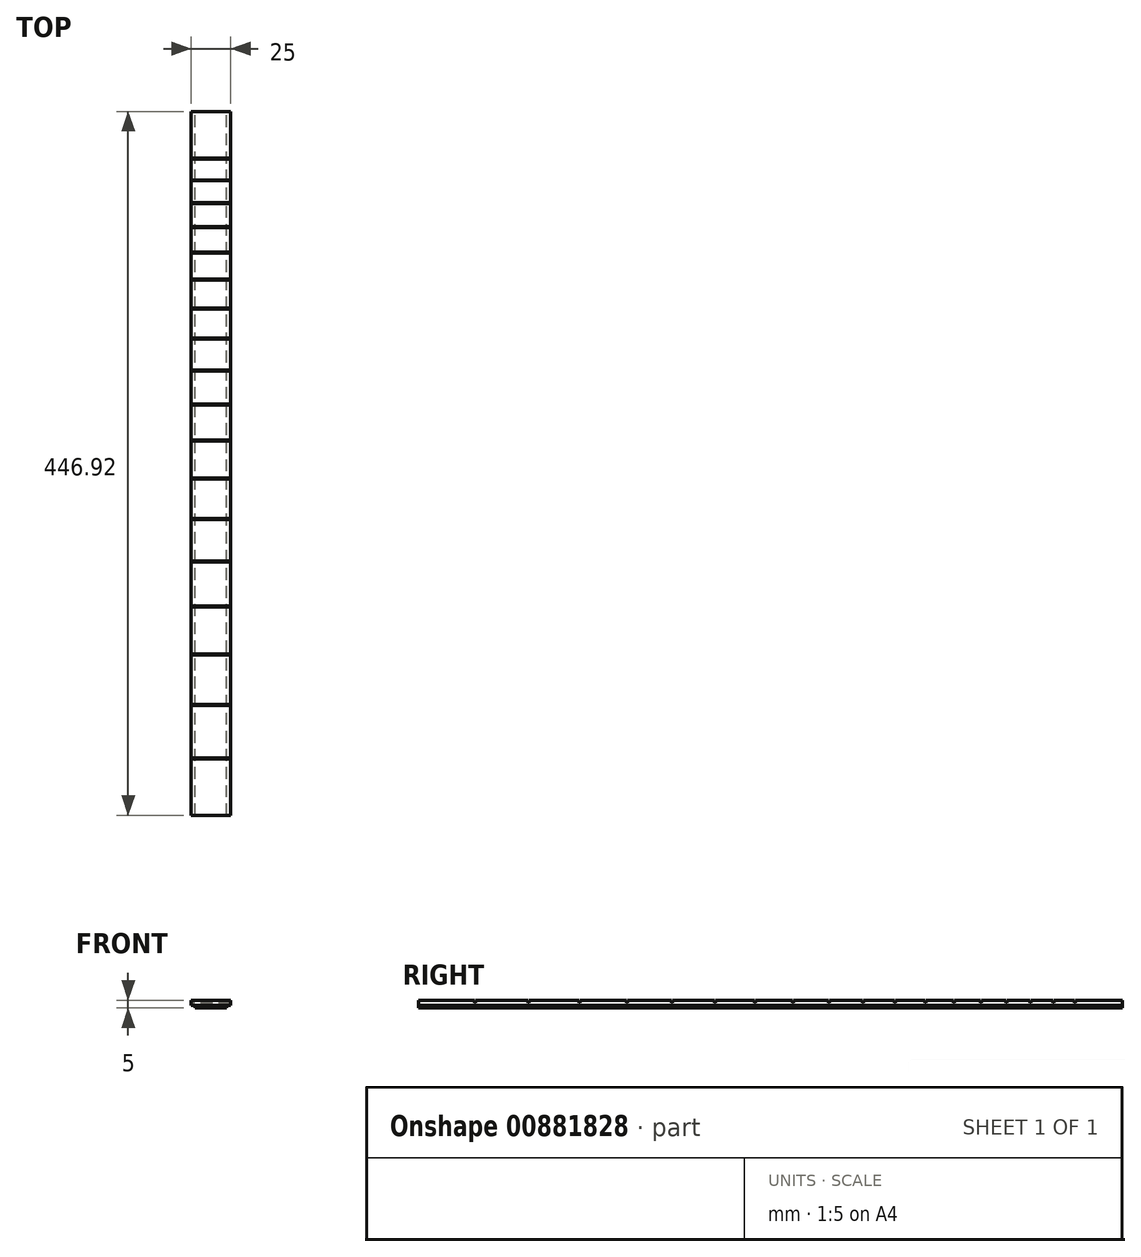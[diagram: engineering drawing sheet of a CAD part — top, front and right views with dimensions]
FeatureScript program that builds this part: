
annotation { "Feature Type Name" : "Feature", "Feature Type Description" : "" }
export const myFeature = defineFeature(function(context is Context, id is Id, definition is map)
    precondition{}
    {
        {
            var Q0;
            Q0=qCreatedBy(makeId("Right.planeOp"),FACE);
            var sketch = newSketch(context, id + "F0", { "sketchPlane" : qUnion([Q0])});
            skLineSegment(sketch, "E0.bottom", {"start": v(0, 0) * mm, "end": v(446.92, 0) * mm});
            skLineSegment(sketch, "E0.top", {"start": v(0, -5) * mm, "end": v(446.92, -5) * mm});
            skLineSegment(sketch, "E0.left", {"start": v(0, 0) * mm, "end": v(0, -5) * mm});
            skLineSegment(sketch, "E1", {"start": v(0, 0) * mm, "end": v(0, 36) * mm, "construction": true});
            skLineSegment(sketch, "E2", {"start": v(0, 36) * mm, "end": v(650, 0) * mm, "construction": true});
            skArc(sketch, "E3", {"start": v(0, 36) * mm, "mid": v(25.46, 25.46) * mm, "end": v(36, 0) * mm, "construction": true});
            skArc(sketch, "E4", {"start": v(36, 34) * mm, "mid": v(60.05, 24.05) * mm, "end": v(70, 0) * mm, "construction": true});
            skArc(sketch, "E5", {"start": v(70, 32.12) * mm, "mid": v(92.72, 22.71) * mm, "end": v(102.13, 0) * mm, "construction": true});
            skArc(sketch, "E6", {"start": v(102.13, 30.34) * mm, "mid": v(123.59, 21.46) * mm, "end": v(132.47, 0) * mm, "construction": true});
            skArc(sketch, "E7", {"start": v(132.47, 28.66) * mm, "mid": v(152.74, 20.27) * mm, "end": v(161.14, 0) * mm, "construction": true});
            skArc(sketch, "E8", {"start": v(161.14, 27.08) * mm, "mid": v(180.28, 19.15) * mm, "end": v(188.21, 0) * mm, "construction": true});
            skArc(sketch, "E9", {"start": v(188.21, 25.58) * mm, "mid": v(206.3, 18.08) * mm, "end": v(213.79, 0) * mm, "construction": true});
            skArc(sketch, "E10", {"start": v(213.79, 24.16) * mm, "mid": v(230.87, 17.08) * mm, "end": v(237.95, 0) * mm, "construction": true});
            skArc(sketch, "E11", {"start": v(237.95, 22.82) * mm, "mid": v(254.08, 16.14) * mm, "end": v(260.77, 0) * mm, "construction": true});
            skArc(sketch, "E12", {"start": v(260.77, 21.56) * mm, "mid": v(276.01, 15.24) * mm, "end": v(282.33, 0) * mm, "construction": true});
            skArc(sketch, "E13", {"start": v(282.33, 20.36) * mm, "mid": v(296.72, 14.4) * mm, "end": v(302.69, 0) * mm, "construction": true});
            skArc(sketch, "E14", {"start": v(302.69, 19.24) * mm, "mid": v(316.3, 13.6) * mm, "end": v(321.92, 0) * mm, "construction": true});
            skArc(sketch, "E15", {"start": v(321.92, 18.17) * mm, "mid": v(334.77, 12.85) * mm, "end": v(340.1, 0) * mm, "construction": true});
            skArc(sketch, "E16", {"start": v(340.1, 17.16) * mm, "mid": v(352.23, 12.14) * mm, "end": v(357.26, 0) * mm, "construction": true});
            skArc(sketch, "E17", {"start": v(357.26, 16.21) * mm, "mid": v(368.72, 11.46) * mm, "end": v(373.47, 0) * mm, "construction": true});
            skArc(sketch, "E18", {"start": v(373.47, 15.32) * mm, "mid": v(384.3, 10.83) * mm, "end": v(388.79, 0) * mm, "construction": true});
            skArc(sketch, "E19", {"start": v(388.79, 14.47) * mm, "mid": v(399.02, 10.23) * mm, "end": v(403.25, 0) * mm, "construction": true});
            skArc(sketch, "E20", {"start": v(403.25, 13.67) * mm, "mid": v(412.92, 9.66) * mm, "end": v(416.92, 0) * mm, "construction": true});
            skLineSegment(sketch, "E21", {"start": v(446.92, 0) * mm, "end": v(446.92, -5) * mm});
            skLineSegment(sketch, "E22", {"start": v(0, 0) * mm, "end": v(650, 0) * mm, "construction": true});
            skLineSegment(sketch, "E23.bottom", {"start": v(35.7, 0) * mm, "end": v(36.3, 0) * mm});
            skLineSegment(sketch, "E23.top", {"start": v(35.7, -1.8) * mm, "end": v(36.3, -1.8) * mm});
            skLineSegment(sketch, "E23.left", {"start": v(35.7, 0) * mm, "end": v(35.7, -1.8) * mm});
            skLineSegment(sketch, "E23.right", {"start": v(36.3, 0) * mm, "end": v(36.3, -1.8) * mm});
            skLineSegment(sketch, "E24.bottom", {"start": v(69.7, 0) * mm, "end": v(70.3, 0) * mm});
            skLineSegment(sketch, "E24.top", {"start": v(69.7, -1.8) * mm, "end": v(70.3, -1.8) * mm});
            skLineSegment(sketch, "E24.left", {"start": v(69.7, 0) * mm, "end": v(69.7, -1.8) * mm});
            skLineSegment(sketch, "E24.right", {"start": v(70.3, 0) * mm, "end": v(70.3, -1.8) * mm});
            skLineSegment(sketch, "E25.bottom", {"start": v(101.83, 0) * mm, "end": v(102.43, 0) * mm});
            skLineSegment(sketch, "E25.top", {"start": v(101.83, -1.8) * mm, "end": v(102.43, -1.8) * mm});
            skLineSegment(sketch, "E25.left", {"start": v(101.83, 0) * mm, "end": v(101.83, -1.8) * mm});
            skLineSegment(sketch, "E25.right", {"start": v(102.43, 0) * mm, "end": v(102.43, -1.8) * mm});
            skLineSegment(sketch, "E26.bottom", {"start": v(132.17, 0) * mm, "end": v(132.77, 0) * mm});
            skLineSegment(sketch, "E26.top", {"start": v(132.17, -1.8) * mm, "end": v(132.77, -1.8) * mm});
            skLineSegment(sketch, "E26.left", {"start": v(132.17, 0) * mm, "end": v(132.17, -1.8) * mm});
            skLineSegment(sketch, "E26.right", {"start": v(132.77, 0) * mm, "end": v(132.77, -1.8) * mm});
            skLineSegment(sketch, "E27.bottom", {"start": v(160.84, 0) * mm, "end": v(161.44, 0) * mm});
            skLineSegment(sketch, "E27.top", {"start": v(160.84, -1.8) * mm, "end": v(161.44, -1.8) * mm});
            skLineSegment(sketch, "E27.left", {"start": v(160.84, 0) * mm, "end": v(160.84, -1.8) * mm});
            skLineSegment(sketch, "E27.right", {"start": v(161.44, 0) * mm, "end": v(161.44, -1.8) * mm});
            skLineSegment(sketch, "E28.bottom", {"start": v(187.91, 0) * mm, "end": v(188.51, 0) * mm});
            skLineSegment(sketch, "E28.top", {"start": v(187.91, -1.8) * mm, "end": v(188.51, -1.8) * mm});
            skLineSegment(sketch, "E28.left", {"start": v(187.91, 0) * mm, "end": v(187.91, -1.8) * mm});
            skLineSegment(sketch, "E28.right", {"start": v(188.51, 0) * mm, "end": v(188.51, -1.8) * mm});
            skLineSegment(sketch, "E29.bottom", {"start": v(213.49, 0) * mm, "end": v(214.09, 0) * mm});
            skLineSegment(sketch, "E29.top", {"start": v(213.49, -1.8) * mm, "end": v(214.09, -1.8) * mm});
            skLineSegment(sketch, "E29.left", {"start": v(213.49, 0) * mm, "end": v(213.49, -1.8) * mm});
            skLineSegment(sketch, "E29.right", {"start": v(214.09, 0) * mm, "end": v(214.09, -1.8) * mm});
            skLineSegment(sketch, "E30.bottom", {"start": v(237.65, 0) * mm, "end": v(238.25, 0) * mm});
            skLineSegment(sketch, "E30.top", {"start": v(237.65, -1.8) * mm, "end": v(238.25, -1.8) * mm});
            skLineSegment(sketch, "E30.left", {"start": v(237.65, 0) * mm, "end": v(237.65, -1.8) * mm});
            skLineSegment(sketch, "E30.right", {"start": v(238.25, 0) * mm, "end": v(238.25, -1.8) * mm});
            skLineSegment(sketch, "E31.bottom", {"start": v(260.47, 0) * mm, "end": v(261.07, 0) * mm});
            skLineSegment(sketch, "E31.top", {"start": v(260.47, -1.8) * mm, "end": v(261.07, -1.8) * mm});
            skLineSegment(sketch, "E31.left", {"start": v(260.47, 0) * mm, "end": v(260.47, -1.8) * mm});
            skLineSegment(sketch, "E31.right", {"start": v(261.07, 0) * mm, "end": v(261.07, -1.8) * mm});
            skLineSegment(sketch, "E32.bottom", {"start": v(282.03, 0) * mm, "end": v(282.63, 0) * mm});
            skLineSegment(sketch, "E32.top", {"start": v(282.03, -1.8) * mm, "end": v(282.63, -1.8) * mm});
            skLineSegment(sketch, "E32.left", {"start": v(282.03, 0) * mm, "end": v(282.03, -1.8) * mm});
            skLineSegment(sketch, "E32.right", {"start": v(282.63, 0) * mm, "end": v(282.63, -1.8) * mm});
            skLineSegment(sketch, "E33.bottom", {"start": v(302.39, 0) * mm, "end": v(302.99, 0) * mm});
            skLineSegment(sketch, "E33.top", {"start": v(302.39, -1.8) * mm, "end": v(302.99, -1.8) * mm});
            skLineSegment(sketch, "E33.left", {"start": v(302.39, 0) * mm, "end": v(302.39, -1.8) * mm});
            skLineSegment(sketch, "E33.right", {"start": v(302.99, 0) * mm, "end": v(302.99, -1.8) * mm});
            skLineSegment(sketch, "E34.bottom", {"start": v(321.62, 0) * mm, "end": v(322.22, 0) * mm});
            skLineSegment(sketch, "E34.top", {"start": v(321.62, -1.8) * mm, "end": v(322.22, -1.8) * mm});
            skLineSegment(sketch, "E34.left", {"start": v(321.62, 0) * mm, "end": v(321.62, -1.8) * mm});
            skLineSegment(sketch, "E34.right", {"start": v(322.22, 0) * mm, "end": v(322.22, -1.8) * mm});
            skLineSegment(sketch, "E35.bottom", {"start": v(339.8, 0) * mm, "end": v(340.4, 0) * mm});
            skLineSegment(sketch, "E35.top", {"start": v(339.8, -1.8) * mm, "end": v(340.4, -1.8) * mm});
            skLineSegment(sketch, "E35.left", {"start": v(339.8, 0) * mm, "end": v(339.8, -1.8) * mm});
            skLineSegment(sketch, "E35.right", {"start": v(340.4, 0) * mm, "end": v(340.4, -1.8) * mm});
            skLineSegment(sketch, "E36.bottom", {"start": v(356.96, 0) * mm, "end": v(357.56, 0) * mm});
            skLineSegment(sketch, "E36.top", {"start": v(356.96, -1.8) * mm, "end": v(357.56, -1.8) * mm});
            skLineSegment(sketch, "E36.left", {"start": v(356.96, 0) * mm, "end": v(356.96, -1.8) * mm});
            skLineSegment(sketch, "E36.right", {"start": v(357.56, 0) * mm, "end": v(357.56, -1.8) * mm});
            skLineSegment(sketch, "E37.bottom", {"start": v(373.17, 0) * mm, "end": v(373.77, 0) * mm});
            skLineSegment(sketch, "E37.top", {"start": v(373.17, -1.8) * mm, "end": v(373.77, -1.8) * mm});
            skLineSegment(sketch, "E37.left", {"start": v(373.17, 0) * mm, "end": v(373.17, -1.8) * mm});
            skLineSegment(sketch, "E37.right", {"start": v(373.77, 0) * mm, "end": v(373.77, -1.8) * mm});
            skLineSegment(sketch, "E38.bottom", {"start": v(388.49, 0) * mm, "end": v(389.09, 0) * mm});
            skLineSegment(sketch, "E38.top", {"start": v(388.49, -1.8) * mm, "end": v(389.09, -1.8) * mm});
            skLineSegment(sketch, "E38.left", {"start": v(388.49, 0) * mm, "end": v(388.49, -1.8) * mm});
            skLineSegment(sketch, "E38.right", {"start": v(389.09, 0) * mm, "end": v(389.09, -1.8) * mm});
            skLineSegment(sketch, "E39.bottom", {"start": v(416.62, 0) * mm, "end": v(417.22, 0) * mm});
            skLineSegment(sketch, "E39.top", {"start": v(416.62, -1.8) * mm, "end": v(417.22, -1.8) * mm});
            skLineSegment(sketch, "E39.left", {"start": v(416.62, 0) * mm, "end": v(416.62, -1.8) * mm});
            skLineSegment(sketch, "E39.right", {"start": v(417.22, 0) * mm, "end": v(417.22, -1.8) * mm});
            skLineSegment(sketch, "E40.bottom", {"start": v(402.95, 0) * mm, "end": v(403.55, 0) * mm});
            skLineSegment(sketch, "E40.top", {"start": v(402.95, -1.8) * mm, "end": v(403.55, -1.8) * mm});
            skLineSegment(sketch, "E40.left", {"start": v(402.95, 0) * mm, "end": v(402.95, -1.8) * mm});
            skLineSegment(sketch, "E40.right", {"start": v(403.55, 0) * mm, "end": v(403.55, -1.8) * mm});
            skLineSegment(sketch, "E41", {"start": v(0, -3.18) * mm, "end": v(446.92, -3.18) * mm});
            skSolve(sketch);
        }
        {
            var Q0;
            Q0=makeQuery(id+"F0.imprint","IMPRINT",FACE,{"disambiguationData":[TD([[makeQuery(id+"F0.imprint","IMPRINT",EDGE,{"derivedFrom":sQuery(id+"F0.wireOp",EDGE,"E23.top")}),-1.0]])]});
            extrude(context, id + "F1", {"entities" : qUnion([Q0]), "endBound" : BoundingType.SYMMETRIC, "depth" : 25 * mm, "offsetDistance" : 25 * mm});
        }
        {
            var Q0;
            {var subQ0=sQuery(id+"F0.wireOp",EDGE,"E0.top");Q0=makeQuery(id+"F0.imprint","IMPRINT",FACE,{"disambiguationData":[TD([[makeQuery(id+"F0.imprint","IMPRINT",EDGE,{"derivedFrom":subQ0}),1.0]])]});}
            extrude(context, id + "F2", {"entities" : qUnion([Q0]), "endBound" : BoundingType.SYMMETRIC, "depth" : 20 * mm, "offsetDistance" : 25 * mm});
        }
    });
